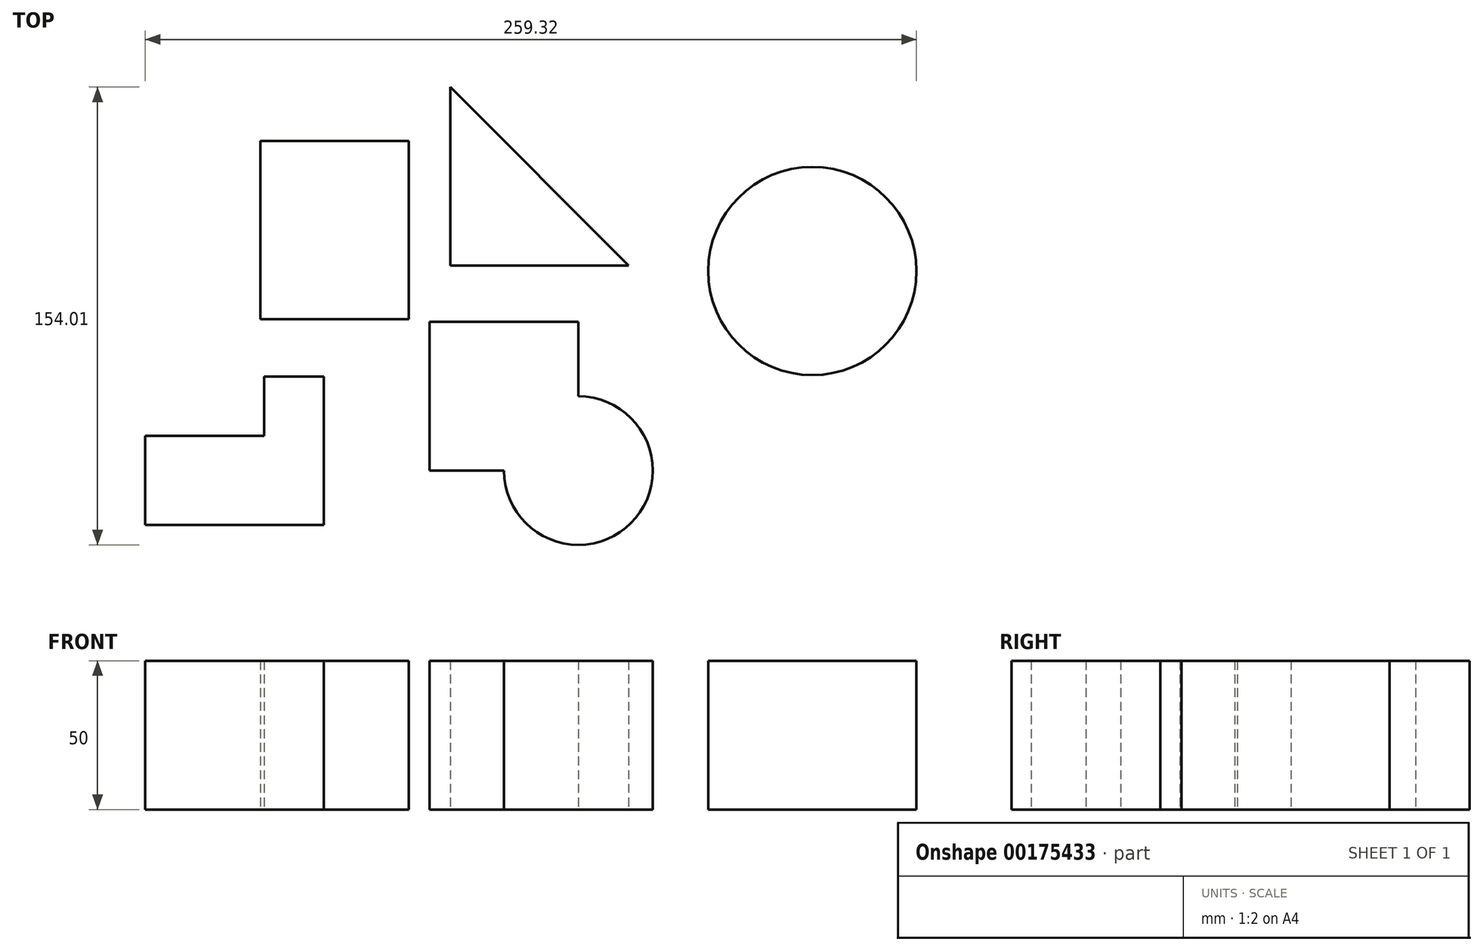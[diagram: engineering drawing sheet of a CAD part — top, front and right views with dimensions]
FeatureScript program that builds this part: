
annotation { "Feature Type Name" : "Feature", "Feature Type Description" : "" }
export const myFeature = defineFeature(function(context is Context, id is Id, definition is map)
    precondition{}
    {
        {
            var Q0;
            Q0=qCreatedBy(makeId("Top.planeOp"),FACE);
            var sketch = newSketch(context, id + "F0", { "sketchPlane" : qUnion([Q0])});
            skLineSegment(sketch, "E0.bottom", {"start": v(-43.6, 43.77) * mm, "end": v(6.4, 43.77) * mm});
            skLineSegment(sketch, "E0.top", {"start": v(-43.6, -16.23) * mm, "end": v(6.4, -16.23) * mm});
            skLineSegment(sketch, "E0.left", {"start": v(-43.6, 43.77) * mm, "end": v(-43.6, -16.23) * mm});
            skLineSegment(sketch, "E0.right", {"start": v(6.4, 43.77) * mm, "end": v(6.4, -16.23) * mm});
            skSolve(sketch);
        }
        {
            var Q0;
            Q0=makeQuery(id+"F0.imprint","IMPRINT",FACE,{"disambiguationData":[TD([[makeQuery(id+"F0.imprint","IMPRINT",EDGE,{"derivedFrom":sQuery(id+"F0.wireOp",EDGE,"E0.bottom")}),-1.0]])]});
            extrude(context, id + "F1", {"entities" : qUnion([Q0]), "depth" : 50 * mm});
        }
        {
            var Q0;
            Q0=qCreatedBy(makeId("Top.planeOp"),FACE);
            var sketch = newSketch(context, id + "F2", { "sketchPlane" : qUnion([Q0])});
            skLineSegment(sketch, "E1", {"start": v(-42.27, -35.48) * mm, "end": v(-22.27, -35.48) * mm});
            skLineSegment(sketch, "E2", {"start": v(-22.27, -35.48) * mm, "end": v(-22.27, -85.48) * mm});
            skLineSegment(sketch, "E3", {"start": v(-22.27, -85.48) * mm, "end": v(-82.27, -85.48) * mm});
            skLineSegment(sketch, "E4", {"start": v(-82.27, -85.48) * mm, "end": v(-82.27, -55.48) * mm});
            skLineSegment(sketch, "E5", {"start": v(-82.27, -55.48) * mm, "end": v(-42.27, -55.48) * mm});
            skLineSegment(sketch, "E6", {"start": v(-42.27, -55.48) * mm, "end": v(-42.27, -35.48) * mm});
            skSolve(sketch);
        }
        {
            var Q0;
            Q0=makeQuery(id+"F2.imprint","IMPRINT",FACE,{"disambiguationData":[TD([[makeQuery(id+"F2.imprint","IMPRINT",EDGE,{"derivedFrom":sQuery(id+"F2.wireOp",EDGE,"E1")}),-1.0]])]});
            extrude(context, id + "F3", {"entities" : qUnion([Q0]), "depth" : 50 * mm});
        }
        {
            var Q0;
            Q0=qCreatedBy(makeId("Top.planeOp"),FACE);
            var sketch = newSketch(context, id + "F4", { "sketchPlane" : qUnion([Q0])});
            skLineSegment(sketch, "E7.top", {"start": v(20.3, 1.88) * mm, "end": v(80.3, 1.88) * mm});
            skLineSegment(sketch, "E7.left", {"start": v(20.3, 61.88) * mm, "end": v(20.3, 1.88) * mm});
            skLineSegment(sketch, "E8", {"start": v(20.3, 61.88) * mm, "end": v(80.3, 1.88) * mm});
            skSolve(sketch);
        }
        {
            var Q0;
            Q0=makeQuery(id+"F4.imprint","IMPRINT",FACE,{"disambiguationData":[TD([[makeQuery(id+"F4.imprint","IMPRINT",EDGE,{"derivedFrom":sQuery(id+"F4.wireOp",EDGE,"E7.top")}),1.0]])]});
            extrude(context, id + "F5", {"entities" : qUnion([Q0]), "depth" : 50 * mm});
        }
        {
            var Q0;
            Q0=qCreatedBy(makeId("Top.planeOp"),FACE);
            var sketch = newSketch(context, id + "F6", { "sketchPlane" : qUnion([Q0])});
            skLineSegment(sketch, "E9.bottom", {"start": v(13.4, -17.13) * mm, "end": v(63.4, -17.13) * mm});
            skLineSegment(sketch, "E9.top", {"start": v(13.4, -67.13) * mm, "end": v(63.4, -67.13) * mm});
            skLineSegment(sketch, "E9.left", {"start": v(13.4, -17.13) * mm, "end": v(13.4, -67.13) * mm});
            skLineSegment(sketch, "E9.right", {"start": v(63.4, -17.13) * mm, "end": v(63.4, -67.13) * mm});
            skCircle(sketch, "E10", {"center": v(63.4, -67.13) * mm, "radius": 25 * mm});
            skCircle(sketch, "E11", {"center": v(142.05, 0) * mm, "radius": 35 * mm});
            skSolve(sketch);
        }
        {
            var Q0;
            {var subQ0=sQuery(id+"F6.wireOp",EDGE,"E9.right");var subQ1=sQuery(id+"F6.wireOp",EDGE,"E9.top");var subQ2=makeQuery(id+"F6.imprint","INTERSECT",VERTEX,{"derivedFrom":[subQ1,subQ0]});Q0=makeQuery(id+"F6.imprint","IMPRINT",FACE,{"disambiguationData":[TD([[makeQuery(id+"F6.imprint","IMPRINT",EDGE,{"disambiguationData":[TD([[subQ2,1.0]])],"derivedFrom":subQ1}),-1.0]])]});}
            var Q1;
            {var subQ0=sQuery(id+"F6.wireOp",EDGE,"E9.right");var subQ1=sQuery(id+"F6.wireOp",EDGE,"E9.top");var subQ2=makeQuery(id+"F6.imprint","INTERSECT",VERTEX,{"derivedFrom":[subQ1,subQ0]});Q1=makeQuery(id+"F6.imprint","IMPRINT",FACE,{"disambiguationData":[TD([[makeQuery(id+"F6.imprint","IMPRINT",EDGE,{"disambiguationData":[TD([[subQ2,1.0]])],"derivedFrom":subQ1}),1.0]])]});}
            var Q2;
            {var subQ1=sQuery(id+"F6.wireOp",EDGE,"E9.bottom");Q2=makeQuery(id+"F6.imprint","IMPRINT",FACE,{"disambiguationData":[TD([[makeQuery(id+"F6.imprint","IMPRINT",EDGE,{"derivedFrom":subQ1}),-1.0]])]});}
            var Q3;
            Q3=makeQuery(id+"F6.imprint","IMPRINT",FACE,{"disambiguationData":[TD([[makeQuery(id+"F6.imprint","IMPRINT",EDGE,{"derivedFrom":sQuery(id+"F6.wireOp",EDGE,"E11")}),1.0]])]});
            extrude(context, id + "F7", {"entities" : qUnion([Q0, Q1, Q2, Q3]), "depth" : 50 * mm});
        }
    });
